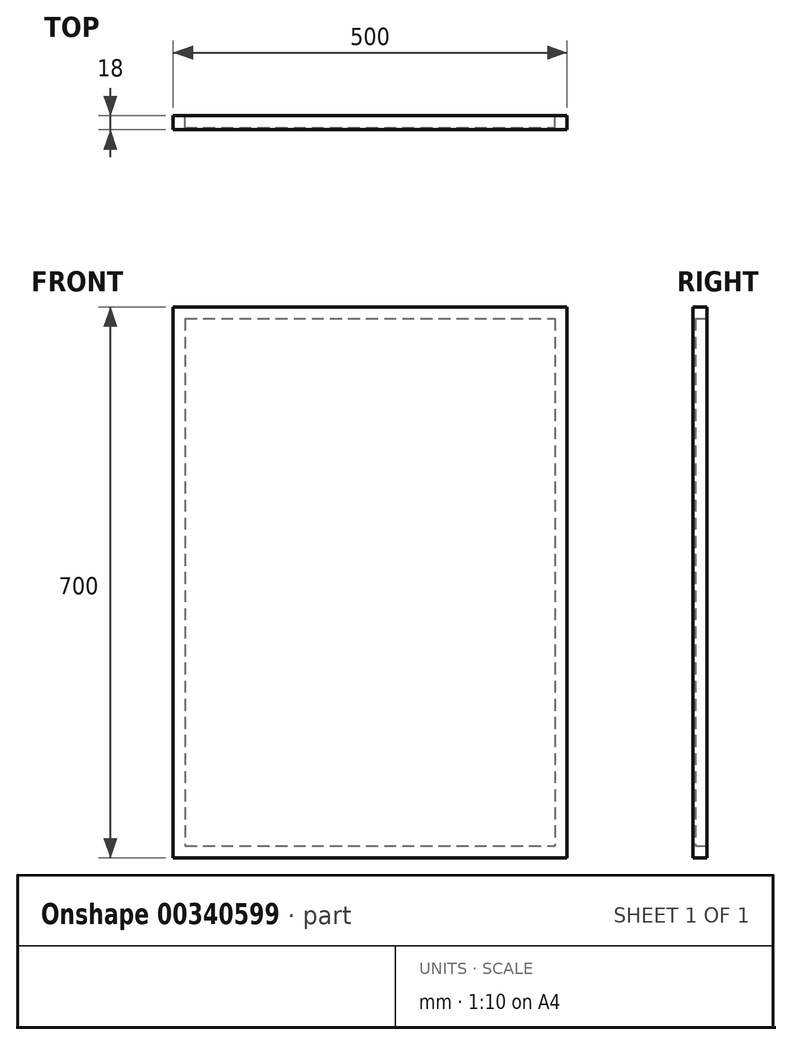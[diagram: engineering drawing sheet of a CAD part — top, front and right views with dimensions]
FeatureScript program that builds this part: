
annotation { "Feature Type Name" : "Feature", "Feature Type Description" : "" }
export const myFeature = defineFeature(function(context is Context, id is Id, definition is map)
    precondition{}
    {
        {
            var Q0;
            Q0=qCreatedBy(makeId("Front.planeOp"),FACE);
            var sketch = newSketch(context, id + "F0", { "sketchPlane" : qUnion([Q0])});
            skLineSegment(sketch, "E0.bottom", {"start": v(-246.25, 370.47) * mm, "end": v(253.75, 370.47) * mm});
            skLineSegment(sketch, "E0.top", {"start": v(-246.25, -329.53) * mm, "end": v(253.75, -329.53) * mm});
            skLineSegment(sketch, "E0.left", {"start": v(-246.25, 370.47) * mm, "end": v(-246.25, -329.53) * mm});
            skLineSegment(sketch, "E0.right", {"start": v(253.75, 370.47) * mm, "end": v(253.75, -329.53) * mm});
            skLineSegment(sketch, "E1.0", {"start": v(-231.25, 355.47) * mm, "end": v(238.75, 355.47) * mm});
            skLineSegment(sketch, "E1.1", {"start": v(-231.25, 355.47) * mm, "end": v(-231.25, -314.53) * mm});
            skLineSegment(sketch, "E1.2", {"start": v(-231.25, -314.53) * mm, "end": v(238.75, -314.53) * mm});
            skLineSegment(sketch, "E1.3", {"start": v(238.75, 355.47) * mm, "end": v(238.75, -314.53) * mm});
            skSolve(sketch);
        }
        {
            var Q0;
            Q0 = qSketchRegion(id + "F0", true);
            extrude(context, id + "F1", {"entities" : qUnion([Q0]), "depth" : 15 * mm});
        }
        {
            var Q0;
            Q0=makeQuery(id+"F1.opExtrude","CAP_FACE",FACE,{"disambiguationData":[OSD([sQuery(id+"F0.wireOp",EDGE,"E0.bottom"),sQuery(id+"F0.wireOp",EDGE,"E0.top"),sQuery(id+"F0.wireOp",EDGE,"E0.left"),sQuery(id+"F0.wireOp",EDGE,"E0.right"),sQuery(id+"F0.wireOp",EDGE,"E1.0"),sQuery(id+"F0.wireOp",EDGE,"E1.1"),sQuery(id+"F0.wireOp",EDGE,"E1.2"),sQuery(id+"F0.wireOp",EDGE,"E1.3")])],"isStart":false});
            var sketch = newSketch(context, id + "F2", { "sketchPlane" : qUnion([Q0])});
            skLineSegment(sketch, "E2.bottom", {"start": v(-246.25, 370.47) * mm, "end": v(253.75, 370.47) * mm});
            skLineSegment(sketch, "E2.top", {"start": v(-246.25, -329.53) * mm, "end": v(253.75, -329.53) * mm});
            skLineSegment(sketch, "E2.left", {"start": v(-246.25, 370.47) * mm, "end": v(-246.25, -329.53) * mm});
            skLineSegment(sketch, "E2.right", {"start": v(253.75, 370.47) * mm, "end": v(253.75, -329.53) * mm});
            skSolve(sketch);
        }
        {
            var Q0;
            Q0 = qSketchRegion(id + "F2", true);
            extrude(context, id + "F3", {"entities" : qUnion([Q0]), "operationType" : NewBodyOperationType.ADD, "depth" : 3 * mm});
        }
    });
